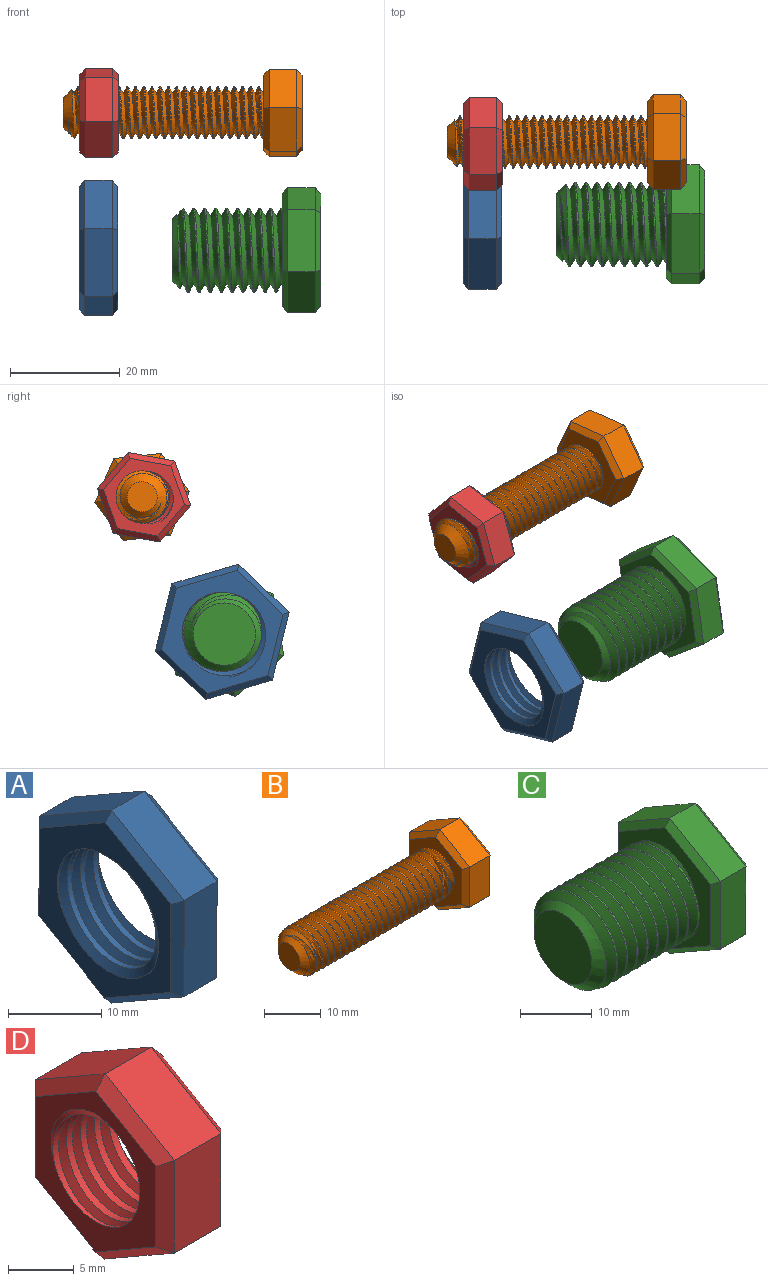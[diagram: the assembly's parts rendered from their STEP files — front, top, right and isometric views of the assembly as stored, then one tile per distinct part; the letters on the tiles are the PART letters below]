
ASSEMBLY  parts=4 mates=2
PART A: 23 faces, bbox 9.3x22.7x26 mm
  f0: cylinder r=7.24mm len=14.48mm, axis (1,0,0), area 111.6mm2, adj f7,f8,f21,f22
  f1: plane 10.98x6.38mm, normal (0,-0.5,0.86), area 63.5mm2, adj f2,f6,f14,f18
  f2: plane 12.7x5mm, normal (0,-1,0), area 63.5mm2, adj f1,f3,f12,f16
  f3: plane 11.02x6.32mm, normal (0,-0.5,-0.87), area 63.5mm2, adj f2,f4,f10,f15
  f4: plane 10.98x6.38mm, normal (0,0.5,-0.86), area 63.5mm2, adj f3,f5,f9,f17
  f5: plane 12.7x5mm, normal (0,1,0), area 63.5mm2, adj f4,f6,f11,f19
  f6: plane 11.02x6.32mm, normal (0,0.5,0.87), area 63.5mm2, adj f1,f5,f13,f20
  f7: plane 23.73x20.67mm, normal (-1,0,0), area 164.4mm2, adj f0,f9,f10,f11,f12,f13,f14,f21
  f8: plane 23.73x20.67mm, normal (1,0,0), area 164.4mm2, adj f0,f15,f16,f17,f18,f19,f20,f21
  f9: plane 10.99x6.96mm, normal (-0.71,0.36,-0.61), area 17.1mm2, adj f4,f7,f10,f11
  f10: plane 11.02x6.9mm, normal (-0.71,-0.35,-0.61), area 17.1mm2, adj f3,f7,f9,f12
  f11: plane 12.7x1.03mm, normal (-0.71,0.71,0), area 17.1mm2, adj f5,f7,f9,f13
  f12: plane 12.7x1.03mm, normal (-0.71,-0.71,0), area 17.1mm2, adj f2,f7,f10,f14
  f13: plane 11.02x6.9mm, normal (-0.71,0.35,0.61), area 17.1mm2, adj f6,f7,f11,f14
  f14: plane 10.99x6.96mm, normal (-0.71,-0.36,0.61), area 17.1mm2, adj f1,f7,f12,f13
  f15: plane 11.02x6.9mm, normal (0.71,-0.35,-0.61), area 17.1mm2, adj f3,f8,f16,f17
  f16: plane 12.7x1.03mm, normal (0.71,-0.71,0), area 17.1mm2, adj f2,f8,f15,f18
  f17: plane 10.99x6.96mm, normal (0.71,0.36,-0.61), area 17.1mm2, adj f4,f8,f15,f19
  f18: plane 10.99x6.96mm, normal (0.71,-0.36,0.61), area 17.1mm2, adj f1,f8,f16,f20
  f19: plane 12.7x1.03mm, normal (0.71,0.71,0), area 17.1mm2, adj f5,f8,f17,f20
  f20: plane 11.02x6.9mm, normal (0.71,0.35,0.61), area 17.1mm2, adj f6,f8,f18,f19
  f21: bspline ~19.31x16.73mm, area 223mm2, adj f0,f7,f8,f22
  f22: bspline ~19.31x16.73mm, area 223mm2, adj f0,f7,f8,f21
PART B: 25 faces, bbox 44.3x15.9x18.1 mm
  f0: cylinder r=4.75mm len=34.5mm, axis (1,0,0), area -4.3mm2, adj f1,f2,f4,f12
  f1: bspline ~36.66x10.97mm, area 807.3mm2, adj f0,f2,f4,f12
  f2: bspline ~37.16x10.97mm, area 806.1mm2, adj f0,f1,f4,f12
  f3: plane 5.5x5.5mm, normal (-1,0,0), area 23.8mm2, adj f4
  f4: cone r=4.75mm half-angle=45deg, axis (1,0,0), area 47.4mm2, adj f0,f1,f2,f3
  f5: plane 7.48x5mm, normal (0,-0.5,0.86), area 43.3mm2, adj f6,f10,f18,f22
  f6: plane 8.66x5mm, normal (0,-1,0), area 43.3mm2, adj f5,f7,f16,f20
  f7: plane 7.52x5mm, normal (0,-0.5,-0.87), area 43.3mm2, adj f6,f8,f14,f19
  f8: plane 7.48x5mm, normal (0,0.5,-0.86), area 43.3mm2, adj f7,f9,f13,f21
  f9: plane 8.66x5mm, normal (0,1,0), area 43.3mm2, adj f8,f10,f15,f23
  f10: plane 7.52x5mm, normal (0,0.5,0.87), area 43.3mm2, adj f5,f9,f17,f24
  f11: plane 15.01x13.03mm, normal (1,0,0), area 146.4mm2, adj f13,f14,f15,f16,f17,f18
  f12: plane 15.83x13.85mm, normal (-1,0,0), area 89.2mm2, adj f0,f1,f2,f19,f20,f21,f22,f23
  f13: plane 7.49x4.93mm, normal (0.71,0.36,-0.61), area 11.4mm2, adj f8,f11,f14,f15
  f14: plane 7.52x4.88mm, normal (0.71,-0.35,-0.61), area 11.4mm2, adj f7,f11,f13,f16
  f15: plane 8.66x1.03mm, normal (0.71,0.71,0), area 11.4mm2, adj f9,f11,f13,f17
  f16: plane 8.66x1.03mm, normal (0.71,-0.71,0), area 11.4mm2, adj f6,f11,f14,f18
  f17: plane 7.52x4.88mm, normal (0.71,0.35,0.61), area 11.4mm2, adj f10,f11,f15,f18
  f18: plane 7.49x4.93mm, normal (0.71,-0.36,0.61), area 11.4mm2, adj f5,f11,f16,f17
  f19: plane 7.52x4.88mm, normal (-0.71,-0.35,-0.61), area 11.4mm2, adj f7,f12,f20,f21
  f20: plane 8.66x1.03mm, normal (-0.71,-0.71,0), area 11.4mm2, adj f6,f12,f19,f22
  f21: plane 7.49x4.93mm, normal (-0.71,0.36,-0.61), area 11.4mm2, adj f8,f12,f19,f23
  f22: plane 7.49x4.93mm, normal (-0.71,-0.36,0.61), area 11.4mm2, adj f5,f12,f20,f24
  f23: plane 8.66x1.03mm, normal (-0.71,0.71,0), area 11.4mm2, adj f9,f12,f21,f24
  f24: plane 7.52x4.88mm, normal (-0.71,0.35,0.61), area 11.4mm2, adj f10,f12,f22,f23
PART C: 26 faces, bbox 27.7x20x23.1 mm
  f0: cylinder r=7.68mm len=18mm, axis (1,0,0), area 139.1mm2, adj f1,f2,f5,f13
  f1: bspline ~20.88x17.74mm, area 713.8mm2, adj f0,f2,f4,f5,f13
  f2: bspline ~21.88x17.74mm, area 715.1mm2, adj f0,f1,f4,f5,f13
  f3: plane 11.36x11.36mm, normal (-1,0,0), area 101.4mm2, adj f4
  f4: cone r=7.68mm half-angle=45deg, axis (1,0,0), area 63.2mm2, adj f1,f2,f3,f5
  f5: cone r=7.68mm half-angle=45deg, axis (1,0,0), area 13.2mm2, adj f0,f1,f2,f4
  f6: plane 9.98x5.81mm, normal (0,-0.5,0.86), area 57.7mm2, adj f7,f11,f19,f23
  f7: plane 11.55x5mm, normal (0,-1,0), area 57.7mm2, adj f6,f8,f17,f21
  f8: plane 10.02x5.74mm, normal (0,-0.5,-0.87), area 57.7mm2, adj f7,f9,f15,f20
  f9: plane 9.98x5.81mm, normal (0,0.5,-0.86), area 57.7mm2, adj f8,f10,f14,f22
  f10: plane 11.55x5mm, normal (0,1,0), area 57.7mm2, adj f9,f11,f16,f24
  f11: plane 10.02x5.74mm, normal (0,0.5,0.87), area 57.7mm2, adj f6,f10,f18,f25
  f12: plane 20.78x18.04mm, normal (1,0,0), area 280.6mm2, adj f14,f15,f16,f17,f18,f19
  f13: plane 20.78x18.04mm, normal (-1,0,0), area 125.2mm2, adj f0,f1,f2,f20,f21,f22,f23,f24
  f14: plane 9.98x6.38mm, normal (0.71,0.36,-0.61), area 15.5mm2, adj f9,f12,f15,f16
  f15: plane 10.02x6.32mm, normal (0.71,-0.35,-0.61), area 15.5mm2, adj f8,f12,f14,f17
  f16: plane 11.55x1.04mm, normal (0.71,0.71,0), area 15.5mm2, adj f10,f12,f14,f18
  f17: plane 11.55x1.04mm, normal (0.71,-0.71,0), area 15.5mm2, adj f7,f12,f15,f19
  f18: plane 10.02x6.32mm, normal (0.71,0.35,0.61), area 15.5mm2, adj f11,f12,f16,f19
  f19: plane 9.98x6.38mm, normal (0.71,-0.36,0.61), area 15.5mm2, adj f6,f12,f17,f18
  f20: plane 10.02x6.32mm, normal (-0.71,-0.35,-0.61), area 15.5mm2, adj f8,f13,f21,f22
  f21: plane 11.55x1.04mm, normal (-0.71,-0.71,0), area 15.5mm2, adj f7,f13,f20,f23
  f22: plane 9.98x6.38mm, normal (-0.71,0.36,-0.61), area 15.5mm2, adj f9,f13,f20,f24
  f23: plane 9.98x6.38mm, normal (-0.71,-0.36,0.61), area 15.5mm2, adj f6,f13,f21,f25
  f24: plane 11.55x1.04mm, normal (-0.71,0.71,0), area 15.5mm2, adj f10,f13,f22,f25
  f25: plane 10.02x6.32mm, normal (-0.71,0.35,0.61), area 15.5mm2, adj f11,f13,f23,f24
PART D: 23 faces, bbox 9.1x15.4x17.7 mm
  f0: plane 7.49x5mm, normal (0,-0.5,0.86), area 43.3mm2, adj f1,f5,f13,f17
  f1: plane 8.66x5mm, normal (0,-1,0), area 43.3mm2, adj f0,f2,f11,f15
  f2: plane 7.51x5mm, normal (0,-0.5,-0.87), area 43.3mm2, adj f1,f3,f9,f14
  f3: plane 7.49x5mm, normal (0,0.5,-0.86), area 43.3mm2, adj f2,f4,f8,f16
  f4: plane 8.66x5mm, normal (0,1,0), area 43.3mm2, adj f3,f5,f10,f18
  f5: plane 7.51x5mm, normal (0,0.5,0.87), area 43.3mm2, adj f0,f4,f12,f19
  f6: plane 15.37x13.38mm, normal (-1,0,0), area 71.4mm2, adj f8,f9,f10,f11,f12,f13,f20,f21
  f7: plane 15.37x13.38mm, normal (1,0,0), area 71.4mm2, adj f14,f15,f16,f17,f18,f19,f20,f21
  f8: plane 7.49x4.93mm, normal (-0.71,0.36,-0.61), area 11.4mm2, adj f3,f6,f9,f10
  f9: plane 7.51x4.89mm, normal (-0.71,-0.35,-0.61), area 11.4mm2, adj f2,f6,f8,f11
  f10: plane 8.66x1.02mm, normal (-0.71,0.71,0), area 11.4mm2, adj f4,f6,f8,f12
  f11: plane 8.66x1.02mm, normal (-0.71,-0.71,0), area 11.4mm2, adj f1,f6,f9,f13
  f12: plane 7.51x4.89mm, normal (-0.71,0.35,0.61), area 11.4mm2, adj f5,f6,f10,f13
  f13: plane 7.49x4.93mm, normal (-0.71,-0.36,0.61), area 11.4mm2, adj f0,f6,f11,f12
  f14: plane 7.51x4.89mm, normal (0.71,-0.35,-0.61), area 11.4mm2, adj f2,f7,f15,f16
  f15: plane 8.66x1.02mm, normal (0.71,-0.71,0), area 11.4mm2, adj f1,f7,f14,f17
  f16: plane 7.49x4.93mm, normal (0.71,0.36,-0.61), area 11.4mm2, adj f3,f7,f14,f18
  f17: plane 7.49x4.93mm, normal (0.71,-0.36,0.61), area 11.4mm2, adj f0,f7,f15,f19
  f18: plane 8.66x1.02mm, normal (0.71,0.71,0), area 11.4mm2, adj f4,f7,f16,f19
  f19: plane 7.51x4.89mm, normal (0.71,0.35,0.61), area 11.4mm2, adj f5,f7,f17,f18
  f20: cylinder r=4.66mm len=9.32mm, axis (1,0,0), area 85.4mm2, adj f6,f7,f21,f22
  f21: bspline ~12.5x10.82mm, area 128.4mm2, adj f6,f7,f20,f22
  f22: bspline ~12.5x10.82mm, area 128.5mm2, adj f6,f7,f20,f21
PLACE A rot(axis=(0,0.6,-0.8),180deg) t=(-55.27,-6.86,23.48)mm fixed
PLACE B rot(axis=(1,0,0),143.4deg) t=(-18.16,7.73,48.08)mm
PLACE C rot(axis=(1,0,0),109.9deg) t=(-14.77,-7.25,23.06)mm
PLACE D rot(axis=(1,0,0),100.2deg) t=(-48.16,7.38,48.02)mm fixed
MATE cylindrical C.f0 <-> A.f7  axis (-1,0,0) through (-38.27,-7.25,23.06)mm
MATE cylindrical B.f0 <-> D.f6  axis (-1,0,0) through (-58.16,7.73,48.08)mm
